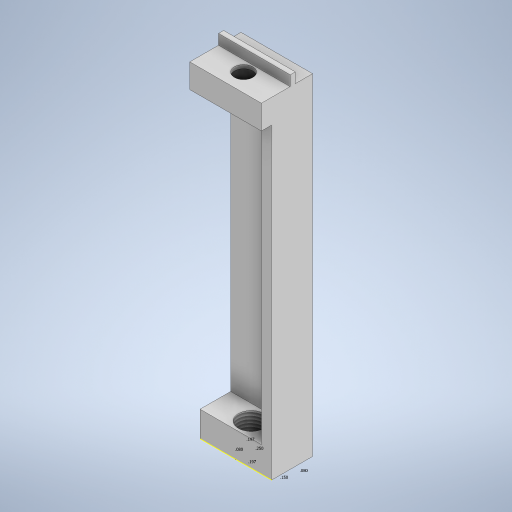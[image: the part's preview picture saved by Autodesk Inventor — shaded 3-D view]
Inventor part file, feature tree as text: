
AUTODESK INVENTOR PART (.ipt)
format: ipt  version: 2024.2 (Build 282272000, 272)  size: 336,896 bytes
history: native  units: in
note: dims shown in document units (in); Inventor stores cm internally (conversion verified against a paired STEP export)
features: extrude x8, sketch x7, thread x1
ambient origin geometry x8: Origin, YZ Plane, XZ Plane, XY Plane, X Axis, Y Axis, Z Axis, Center Point
bodies: Solid1 (feature_tree)
feature tree (16):
  extrude  "Extrusion1"  Depth=0.4in
  sketch  "Sketch2"  dims[d2=3.24in d3=0.0in d5=0.25in]
  extrude  "Extrusion2"  Depth=0.25in
  extrude  "Extrusion3"  Depth=0.197in
  extrude  "Extrusion4"  Depth=0.08in
  thread  "Thread1"  [1 undecoded]
  sketch  "Sketch4"  dims[d8=0.08in d9=0.08in d10=2.0in d11=0.0in]
  sketch  "Sketch5"  dims[d12=0.25in d13=0.6in]
  extrude  "Extrusion7"  Depth=0.6in
  extrude  "Extrusion8"  Depth=0.175in TaperAngle=0.0deg
  extrude  "Extrusion9"  Depth=0.15in
  extrude  "Extrusion10"  Depth=0.2in
  sketch  "Sketch1"  dims[d0=0.7in d1=0.4in]
  sketch  "Sketch3"  dims[d6=0.197in d7=0.197in]
  sketch  "Sketch6"  dims[d14=0.3in d15=0.0in d16=0.175in d17=0.0in]
  sketch  "Sketch8"  dims[d18=0.3896in d19=0.0in d20=0.15in d21=0.18in d24=0.105in d25=0.05in d28=0.074in d29=0.18in d30=0.1in d31=0.2352in d32=0.0in d33=1.0in d34=0.0in d35=0.074in d36=0.074in d37=0.05in d38=0.1in d39=0.0in d41=0.3in d42=0.2in d43=0.0in]
note: 1 required parameter value undecoded (feature->parameter linkage not recoverable at this tier; creation-order binding heuristic only, values carry confidence <= 0.55)
